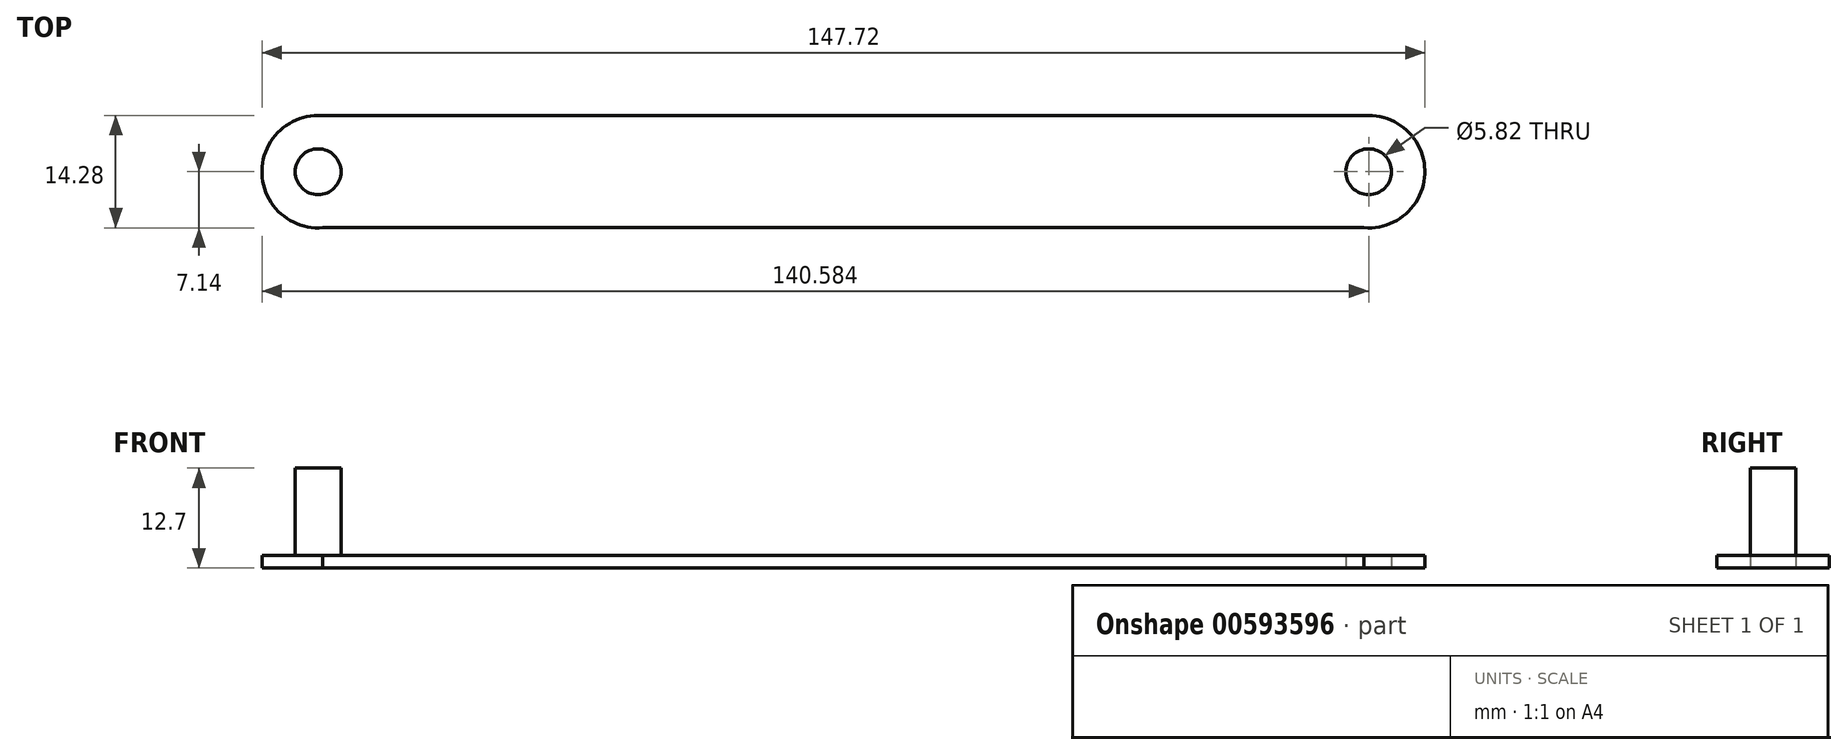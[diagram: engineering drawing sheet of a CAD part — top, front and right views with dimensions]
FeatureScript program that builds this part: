
annotation { "Feature Type Name" : "Feature", "Feature Type Description" : "" }
export const myFeature = defineFeature(function(context is Context, id is Id, definition is map)
    precondition{}
    {
        {
            var Q0;
            Q0=qCreatedBy(makeId("Top.planeOp"),FACE);
            var sketch = newSketch(context, id + "F0", { "sketchPlane" : qUnion([Q0])});
            skCircle(sketch, "E0", {"center": v(-66.72, 0) * mm, "radius": 7.14 * mm});
            skCircle(sketch, "E1.MirrorC", {"center": v(66.72, 0) * mm, "radius": 7.14 * mm});
            skLineSegment(sketch, "E2", {"start": v(-66.72, 7.14) * mm, "end": v(66.72, 7.14) * mm});
            skLineSegment(sketch, "E3", {"start": v(-66.14, -7.11) * mm, "end": v(66.14, -7.11) * mm});
            skCircle(sketch, "E4", {"center": v(-66.72, 0) * mm, "radius": 2.9 * mm});
            skCircle(sketch, "E5.MirrorC", {"center": v(66.72, 0) * mm, "radius": 2.9 * mm});
            skSolve(sketch);
        }
        {
            var Q0;
            Q0 = qSketchRegion(id + "F0", true);
            extrude(context, id + "F1", {"entities" : qUnion([Q0]), "depth" : 1.59 * mm, "offsetDistance" : 25.4 * mm});
        }
        {
            var Q0;
            Q0=makeQuery(id+"F0.imprint","IMPRINT",FACE,{"disambiguationData":[TD([[makeQuery(id+"F0.imprint","IMPRINT",EDGE,{"derivedFrom":sQuery(id+"F0.wireOp",EDGE,"E4")}),1.0]])]});
            extrude(context, id + "F2", {"entities" : qUnion([Q0]), "operationType" : NewBodyOperationType.ADD, "depth" : 12.7 * mm, "offsetDistance" : 25.4 * mm});
        }
    });
